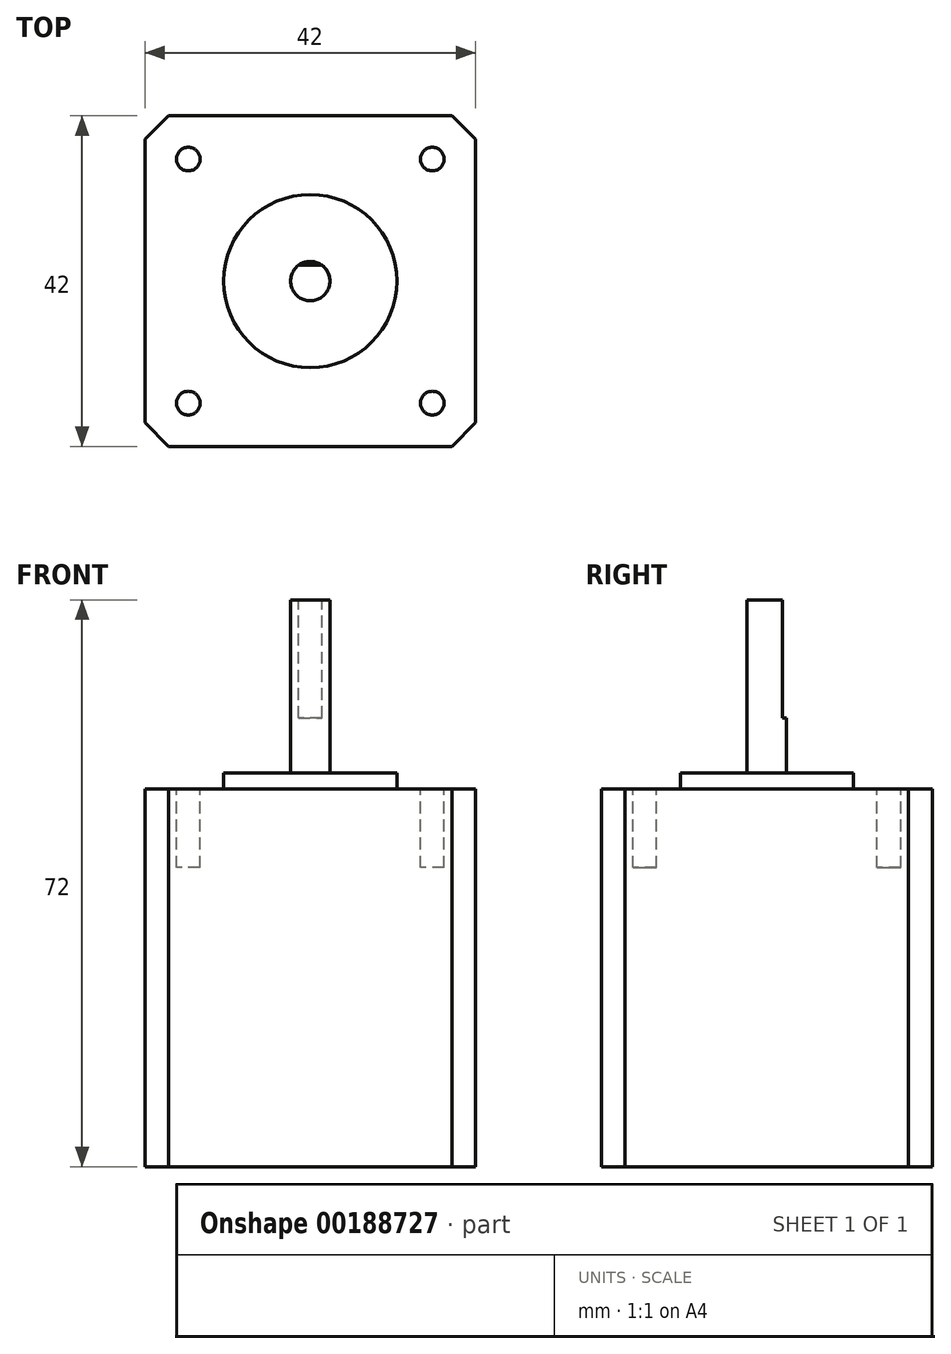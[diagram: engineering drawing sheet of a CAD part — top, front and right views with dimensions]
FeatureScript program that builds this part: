
annotation { "Feature Type Name" : "Feature", "Feature Type Description" : "" }
export const myFeature = defineFeature(function(context is Context, id is Id, definition is map)
    precondition{}
    {
        {
            var Q0;
            Q0=qCreatedBy(makeId("Top.planeOp"),FACE);
            var sketch = newSketch(context, id + "F0", { "sketchPlane" : qUnion([Q0])});
            skLineSegment(sketch, "E0.bottom", {"start": v(21, -21) * mm, "end": v(-21, -21) * mm});
            skLineSegment(sketch, "E0.top", {"start": v(21, 21) * mm, "end": v(-21, 21) * mm});
            skLineSegment(sketch, "E0.left", {"start": v(21, -21) * mm, "end": v(21, 21) * mm});
            skLineSegment(sketch, "E0.right", {"start": v(-21, -21) * mm, "end": v(-21, 21) * mm});
            skPoint(sketch, "E0.middle", {"position": v(0, 0) * mm});
            skSolve(sketch);
        }
        {
            var Q0;
            Q0=makeQuery(id+"F0.imprint","IMPRINT",FACE,{"disambiguationData":[TD([[makeQuery(id+"F0.imprint","IMPRINT",EDGE,{"derivedFrom":sQuery(id+"F0.wireOp",EDGE,"E0.bottom")}),-1.0]])]});
            extrude(context, id + "F1", {"entities" : qUnion([Q0]), "depth" : 48 * mm});
        }
        {
            var Q0;
            Q0=makeQuery(id+"F1.opExtrude","CAP_FACE",FACE,{"disambiguationData":[OSD([sQuery(id+"F0.wireOp",EDGE,"E0.bottom"),sQuery(id+"F0.wireOp",EDGE,"E0.top"),sQuery(id+"F0.wireOp",EDGE,"E0.left"),sQuery(id+"F0.wireOp",EDGE,"E0.right")])],"isStart":false});
            var sketch = newSketch(context, id + "F2", { "sketchPlane" : qUnion([Q0])});
            skLineSegment(sketch, "E1.bottom", {"start": v(15.5, 15.5) * mm, "end": v(-15.5, 15.5) * mm, "construction": true});
            skLineSegment(sketch, "E1.top", {"start": v(15.5, -15.5) * mm, "end": v(-15.5, -15.5) * mm, "construction": true});
            skLineSegment(sketch, "E1.left", {"start": v(15.5, 15.5) * mm, "end": v(15.5, -15.5) * mm, "construction": true});
            skLineSegment(sketch, "E1.right", {"start": v(-15.5, 15.5) * mm, "end": v(-15.5, -15.5) * mm, "construction": true});
            skPoint(sketch, "E1.middle", {"position": v(0, 0) * mm});
            skCircle(sketch, "E2", {"center": v(-15.5, 15.5) * mm, "radius": 1.5 * mm});
            skCircle(sketch, "E3", {"center": v(-15.5, -15.5) * mm, "radius": 1.5 * mm});
            skCircle(sketch, "E4", {"center": v(15.5, 15.5) * mm, "radius": 1.5 * mm});
            skCircle(sketch, "E5", {"center": v(15.5, -15.5) * mm, "radius": 1.5 * mm});
            skCircle(sketch, "E6", {"center": v(0, 0) * mm, "radius": 11 * mm});
            skSolve(sketch);
        }
        {
            var Q0;
            Q0=makeQuery(id+"F2.imprint","IMPRINT",FACE,{"disambiguationData":[TD([[makeQuery(id+"F2.imprint","IMPRINT",EDGE,{"derivedFrom":sQuery(id+"F2.wireOp",EDGE,"E3")}),1.0]])]});
            var Q1;
            Q1=makeQuery(id+"F2.imprint","IMPRINT",FACE,{"disambiguationData":[TD([[makeQuery(id+"F2.imprint","IMPRINT",EDGE,{"derivedFrom":sQuery(id+"F2.wireOp",EDGE,"E2")}),1.0]])]});
            var Q2;
            Q2=makeQuery(id+"F2.imprint","IMPRINT",FACE,{"disambiguationData":[TD([[makeQuery(id+"F2.imprint","IMPRINT",EDGE,{"derivedFrom":sQuery(id+"F2.wireOp",EDGE,"E4")}),1.0]])]});
            var Q3;
            Q3=makeQuery(id+"F2.imprint","IMPRINT",FACE,{"disambiguationData":[TD([[makeQuery(id+"F2.imprint","IMPRINT",EDGE,{"derivedFrom":sQuery(id+"F2.wireOp",EDGE,"E5")}),1.0]])]});
            var Q4;
            Q4=sQuery(id+"F2.wireOp",EDGE,"E2");
            var Q5;
            Q5=sQuery(id+"F2.wireOp",EDGE,"E3");
            var Q6;
            Q6=sQuery(id+"F2.wireOp",EDGE,"E5");
            var Q7;
            Q7=sQuery(id+"F2.wireOp",EDGE,"E4");
            extrude(context, id + "F3", {"entities" : qUnion([Q0, Q1, Q2, Q3]), "operationType" : NewBodyOperationType.REMOVE, "surfaceEntities" : qUnion([Q4, Q5, Q6, Q7]), "oppositeDirection" : true, "depth" : 10 * mm});
        }
        {
            var Q0;
            Q0=makeQuery(id+"F2.imprint","IMPRINT",FACE,{"disambiguationData":[TD([[makeQuery(id+"F2.imprint","IMPRINT",EDGE,{"derivedFrom":sQuery(id+"F2.wireOp",EDGE,"E6")}),1.0]])]});
            extrude(context, id + "F4", {"entities" : qUnion([Q0]), "operationType" : NewBodyOperationType.ADD, "depth" : 2 * mm});
        }
        {
            var Q0;
            Q0=makeQuery(id+"F4.opExtrude","CAP_FACE",FACE,{"disambiguationData":[OSD([sQuery(id+"F2.wireOp",EDGE,"E6")])],"isStart":false});
            var sketch = newSketch(context, id + "F5", { "sketchPlane" : qUnion([Q0])});
            skCircle(sketch, "E7", {"center": v(0, 0) * mm, "radius": 2.5 * mm});
            skSolve(sketch);
        }
        {
            var Q0;
            Q0=makeQuery(id+"F5.imprint","IMPRINT",FACE,{"disambiguationData":[TD([[makeQuery(id+"F5.imprint","IMPRINT",EDGE,{"derivedFrom":sQuery(id+"F5.wireOp",EDGE,"E7")}),1.0]])]});
            extrude(context, id + "F6", {"entities" : qUnion([Q0]), "operationType" : NewBodyOperationType.ADD, "depth" : 22 * mm});
        }
        {
            var Q0;
            Q0=makeQuery(id+"F6.opExtrude","CAP_FACE",FACE,{"disambiguationData":[OSD([sQuery(id+"F5.wireOp",EDGE,"E7")])],"isStart":false});
            var sketch = newSketch(context, id + "F7", { "sketchPlane" : qUnion([Q0])});
            skLineSegment(sketch, "E8", {"start": v(-1.5, 2) * mm, "end": v(1.5, 2) * mm});
            skSolve(sketch);
        }
        {
            var Q0;
            {var subQ0=sQuery(id+"F7.wireOp",EDGE,"E8");Q0=makeQuery(id+"F7.imprint","IMPRINT",FACE,{"disambiguationData":[TD([[makeQuery(id+"F7.imprint","IMPRINT",EDGE,{"derivedFrom":subQ0}),1.0]])]});}
            extrude(context, id + "F8", {"entities" : qUnion([Q0]), "operationType" : NewBodyOperationType.REMOVE, "oppositeDirection" : true, "depth" : 15 * mm});
        }
        {
            var Q0;
            Q0=makeQuery(id+"F1.opExtrude","SWEPT_EDGE",EDGE,{"disambiguationData":[OSD([sQuery(id+"F0.wireOp",EDGE,"E0.bottom"),sQuery(id+"F0.wireOp",EDGE,"E0.left")])]});
            var Q1;
            Q1=makeQuery(id+"F1.opExtrude","SWEPT_EDGE",EDGE,{"disambiguationData":[OSD([sQuery(id+"F0.wireOp",EDGE,"E0.top"),sQuery(id+"F0.wireOp",EDGE,"E0.left")])]});
            var Q2;
            Q2=makeQuery(id+"F1.opExtrude","SWEPT_EDGE",EDGE,{"disambiguationData":[OSD([sQuery(id+"F0.wireOp",EDGE,"E0.bottom"),sQuery(id+"F0.wireOp",EDGE,"E0.right")])]});
            var Q3;
            Q3=makeQuery(id+"F1.opExtrude","SWEPT_EDGE",EDGE,{"disambiguationData":[OSD([sQuery(id+"F0.wireOp",EDGE,"E0.top"),sQuery(id+"F0.wireOp",EDGE,"E0.right")])]});
            chamfer(context, id + "F9", {"entities" : qUnion([Q0, Q1, Q2, Q3]), "width" : 3 * mm, "tangentPropagation" : true});
        }
    });
